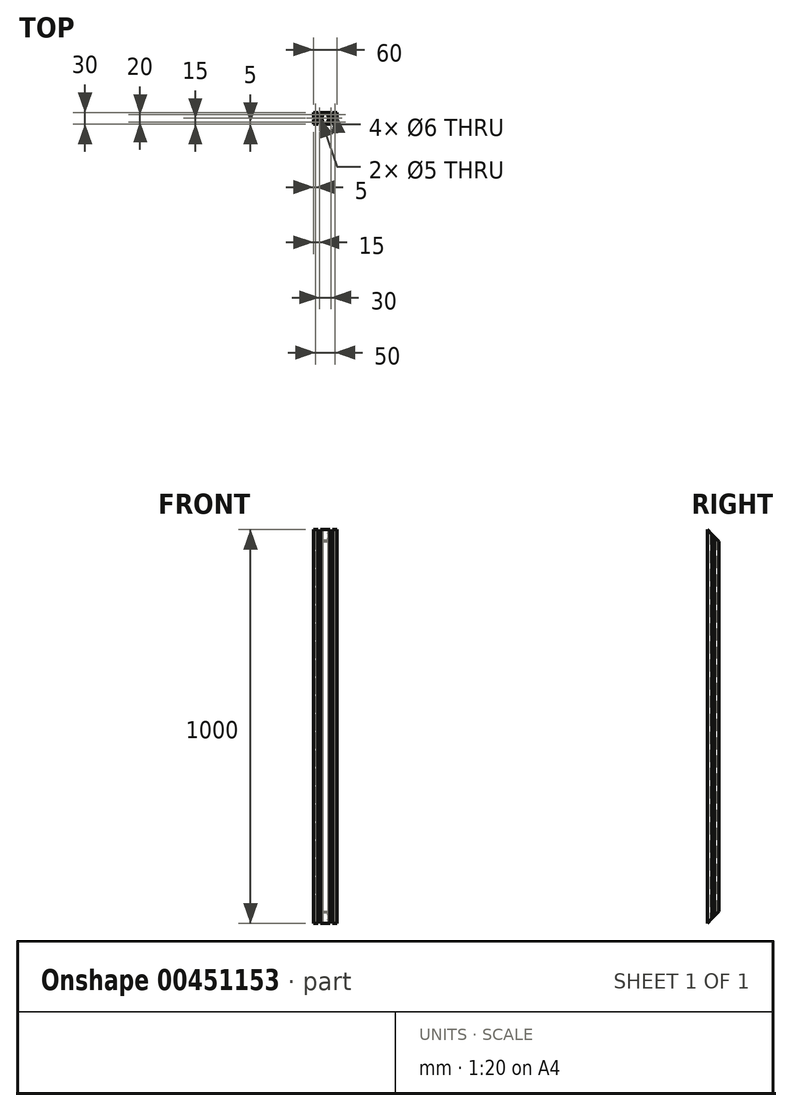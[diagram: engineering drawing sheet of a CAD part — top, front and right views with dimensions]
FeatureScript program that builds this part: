
annotation { "Feature Type Name" : "Feature", "Feature Type Description" : "" }
export const myFeature = defineFeature(function(context is Context, id is Id, definition is map)
    precondition{}
    {
        {
            var Q0;
            Q0=qCreatedBy(makeId("Top.planeOp"),FACE);
            var sketch = newSketch(context, id + "F0", { "sketchPlane" : qUnion([Q0])});
            skLineSegment(sketch, "E0.bottom", {"start": v(30, -15) * mm, "end": v(-30, -15) * mm});
            skLineSegment(sketch, "E0.top", {"start": v(30, 15) * mm, "end": v(-30, 15) * mm});
            skLineSegment(sketch, "E0.left", {"start": v(30, -15) * mm, "end": v(30, 15) * mm});
            skLineSegment(sketch, "E0.right", {"start": v(-30, -15) * mm, "end": v(-30, 15) * mm});
            skPoint(sketch, "E0.middle", {"position": v(0, 0) * mm});
            skLineSegment(sketch, "E1.top", {"start": v(-11.85, 15) * mm, "end": v(-18.15, 15) * mm});
            skLineSegment(sketch, "E1.left", {"start": v(-11.85, 12.5) * mm, "end": v(-11.85, 15) * mm});
            skLineSegment(sketch, "E1.right", {"start": v(-18.15, 12.5) * mm, "end": v(-18.15, 15) * mm});
            skPoint(sketch, "E1.middle", {"position": v(-15, 13.75) * mm});
            skLineSegment(sketch, "E2.bottom", {"start": v(-9.85, 12.5) * mm, "end": v(-11.85, 12.5) * mm});
            skLineSegment(sketch, "E2.left", {"start": v(-9.85, 12.5) * mm, "end": v(-9.85, 6.55) * mm});
            skLineSegment(sketch, "E2.right", {"start": v(-20.15, 12.5) * mm, "end": v(-20.15, 6.55) * mm});
            skPoint(sketch, "E2.middle", {"position": v(-15, 9.52) * mm});
            skArc(sketch, "E3", {"start": v(-20.15, 6.55) * mm, "mid": v(-15, 4.5) * mm, "end": v(-9.85, 6.55) * mm});
            skPoint(sketch, "E4.MirrorP", {"position": v(15, 9.52) * mm});
            skPoint(sketch, "E5.MirrorP", {"position": v(15, 13.75) * mm});
            skLineSegment(sketch, "E6.MirrorCS", {"start": v(11.85, 12.5) * mm, "end": v(11.85, 15) * mm});
            skLineSegment(sketch, "E7.MirrorCS", {"start": v(18.15, 12.5) * mm, "end": v(18.15, 15) * mm});
            skLineSegment(sketch, "E8.MirrorCS", {"start": v(9.85, 12.5) * mm, "end": v(11.85, 12.5) * mm});
            skLineSegment(sketch, "E9.MirrorCS", {"start": v(9.85, 12.5) * mm, "end": v(9.85, 6.55) * mm});
            skArc(sketch, "E10.MirrorCS", {"start": v(20.15, 6.55) * mm, "mid": v(15, 4.5) * mm, "end": v(9.85, 6.55) * mm});
            skLineSegment(sketch, "E11.MirrorCS", {"start": v(20.15, 12.5) * mm, "end": v(20.15, 6.55) * mm});
            skLineSegment(sketch, "E12.MirrorCS", {"start": v(11.85, 15) * mm, "end": v(18.15, 15) * mm});
            skLineSegment(sketch, "E13.trimOffspring", {"start": v(-18.15, 12.5) * mm, "end": v(-20.15, 12.5) * mm});
            skLineSegment(sketch, "E14.trimOffspring", {"start": v(18.15, 12.5) * mm, "end": v(20.15, 12.5) * mm});
            skCircle(sketch, "E15", {"center": v(-15, 0) * mm, "radius": 2.5 * mm});
            skCircle(sketch, "E16", {"center": v(-25, 10) * mm, "radius": 3 * mm});
            skCircle(sketch, "E17.MirrorC", {"center": v(25, 10) * mm, "radius": 3 * mm});
            skCircle(sketch, "E18.MirrorC", {"center": v(25, -10) * mm, "radius": 3 * mm});
            skCircle(sketch, "E19.MirrorC", {"center": v(-25, -10) * mm, "radius": 3 * mm});
            skCircle(sketch, "E20.MirrorC", {"center": v(15, 0) * mm, "radius": 2.5 * mm});
            skLineSegment(sketch, "E21", {"start": v(-7, 12.5) * mm, "end": v(0, 12.5) * mm});
            skLineSegment(sketch, "E22", {"start": v(-7, 12.5) * mm, "end": v(-7, 7) * mm});
            skLineSegment(sketch, "E23", {"start": v(-10, 0) * mm, "end": v(-7, 7) * mm});
            skLineSegment(sketch, "E24.MirrorCS", {"start": v(10, 0) * mm, "end": v(7, 7) * mm});
            skLineSegment(sketch, "E25.MirrorCS", {"start": v(7, 12.5) * mm, "end": v(0, 12.5) * mm});
            skLineSegment(sketch, "E26.MirrorCS", {"start": v(7, 12.5) * mm, "end": v(7, 7) * mm});
            skLineSegment(sketch, "E27.MirrorCS", {"start": v(-18.15, -12.5) * mm, "end": v(-20.15, -12.5) * mm});
            skLineSegment(sketch, "E28.MirrorCS", {"start": v(-9.85, -12.5) * mm, "end": v(-11.85, -12.5) * mm});
            skLineSegment(sketch, "E29.MirrorCS", {"start": v(-9.85, -12.5) * mm, "end": v(-9.85, -6.55) * mm});
            skPoint(sketch, "E30.MirrorP", {"position": v(-15, -13.75) * mm});
            skPoint(sketch, "E31.MirrorP", {"position": v(-15, -9.52) * mm});
            skLineSegment(sketch, "E32.MirrorCS", {"start": v(-18.15, -12.5) * mm, "end": v(-18.15, -15) * mm});
            skLineSegment(sketch, "E33.MirrorCS", {"start": v(-11.85, -15) * mm, "end": v(-18.15, -15) * mm});
            skLineSegment(sketch, "E34.MirrorCS", {"start": v(-20.15, -12.5) * mm, "end": v(-20.15, -6.55) * mm});
            skLineSegment(sketch, "E35.MirrorCS", {"start": v(-11.85, -12.5) * mm, "end": v(-11.85, -15) * mm});
            skArc(sketch, "E36.MirrorCS", {"start": v(-20.15, -6.55) * mm, "mid": v(-15, -4.5) * mm, "end": v(-9.85, -6.55) * mm});
            skLineSegment(sketch, "E37.MirrorCS", {"start": v(18.15, -12.5) * mm, "end": v(20.15, -12.5) * mm});
            skLineSegment(sketch, "E38.MirrorCS", {"start": v(9.85, -12.5) * mm, "end": v(11.85, -12.5) * mm});
            skPoint(sketch, "E39.MirrorP", {"position": v(15, -13.75) * mm});
            skPoint(sketch, "E40.MirrorP", {"position": v(15, -9.52) * mm});
            skLineSegment(sketch, "E41.MirrorCS", {"start": v(18.15, -12.5) * mm, "end": v(18.15, -15) * mm});
            skArc(sketch, "E42.MirrorCS", {"start": v(20.15, -6.55) * mm, "mid": v(15, -4.5) * mm, "end": v(9.85, -6.55) * mm});
            skLineSegment(sketch, "E43.MirrorCS", {"start": v(9.85, -12.5) * mm, "end": v(9.85, -6.55) * mm});
            skLineSegment(sketch, "E44.MirrorCS", {"start": v(11.85, -12.5) * mm, "end": v(11.85, -15) * mm});
            skLineSegment(sketch, "E45.MirrorCS", {"start": v(11.85, -15) * mm, "end": v(18.15, -15) * mm});
            skLineSegment(sketch, "E46.MirrorCS", {"start": v(20.15, -12.5) * mm, "end": v(20.15, -6.55) * mm});
            skLineSegment(sketch, "E47.MirrorCS", {"start": v(10, 0) * mm, "end": v(7, -7) * mm});
            skLineSegment(sketch, "E48.MirrorCS", {"start": v(7, -12.5) * mm, "end": v(7, -7) * mm});
            skLineSegment(sketch, "E49.MirrorCS", {"start": v(7, -12.5) * mm, "end": v(0, -12.5) * mm});
            skLineSegment(sketch, "E50.MirrorCS", {"start": v(-7, -12.5) * mm, "end": v(0, -12.5) * mm});
            skLineSegment(sketch, "E51.MirrorCS", {"start": v(-10, 0) * mm, "end": v(-7, -7) * mm});
            skLineSegment(sketch, "E52.MirrorCS", {"start": v(-7, -12.5) * mm, "end": v(-7, -7) * mm});
            skLineSegment(sketch, "E53.top", {"start": v(-30, 3.15) * mm, "end": v(-30, -3.15) * mm});
            skLineSegment(sketch, "E53.left", {"start": v(-27.5, 3.15) * mm, "end": v(-30, 3.15) * mm});
            skLineSegment(sketch, "E53.right", {"start": v(-27.5, -3.15) * mm, "end": v(-30, -3.15) * mm});
            skLineSegment(sketch, "E54.bottom", {"start": v(-27.5, 5.15) * mm, "end": v(-27.5, 3.15) * mm});
            skLineSegment(sketch, "E54.left", {"start": v(-27.5, 5.15) * mm, "end": v(-21.55, 5.15) * mm});
            skLineSegment(sketch, "E54.right", {"start": v(-27.5, -5.15) * mm, "end": v(-21.55, -5.15) * mm});
            skArc(sketch, "E55", {"start": v(-21.55, -5.15) * mm, "mid": v(-19.5, 0) * mm, "end": v(-21.55, 5.15) * mm});
            skLineSegment(sketch, "E56.trimOffspring", {"start": v(-27.5, -3.15) * mm, "end": v(-27.5, -5.15) * mm});
            skArc(sketch, "E57.MirrorCS", {"start": v(21.55, -5.15) * mm, "mid": v(19.5, 0) * mm, "end": v(21.55, 5.15) * mm});
            skLineSegment(sketch, "E58.MirrorCS", {"start": v(27.5, -5.15) * mm, "end": v(21.55, -5.15) * mm});
            skLineSegment(sketch, "E59.MirrorCS", {"start": v(30, 3.15) * mm, "end": v(30, -3.15) * mm});
            skLineSegment(sketch, "E60.MirrorCS", {"start": v(27.5, -3.15) * mm, "end": v(30, -3.15) * mm});
            skLineSegment(sketch, "E61.MirrorCS", {"start": v(27.5, 5.15) * mm, "end": v(27.5, 3.15) * mm});
            skLineSegment(sketch, "E62.MirrorCS", {"start": v(27.5, 3.15) * mm, "end": v(30, 3.15) * mm});
            skLineSegment(sketch, "E63.MirrorCS", {"start": v(27.5, 5.15) * mm, "end": v(21.55, 5.15) * mm});
            skLineSegment(sketch, "E64.MirrorCS", {"start": v(27.5, -3.15) * mm, "end": v(27.5, -5.15) * mm});
            skSolve(sketch);
        }
        {
            var Q0;
            {var subQ30=sQuery(id+"F0.wireOp",EDGE,"E1.left");Q0=makeQuery(id+"F0.imprint","IMPRINT",FACE,{"disambiguationData":[TD([[makeQuery(id+"F0.imprint","IMPRINT",EDGE,{"derivedFrom":subQ30}),-1.0]])]});}
            extrude(context, id + "F1", {"entities" : qUnion([Q0]), "offsetDistance" : 25 * mm, "depth" : 1000 * mm});
        }
        {
            var Q0;
            Q0=makeQuery(id+"F1.opExtrude","SWEPT_EDGE",EDGE,{"disambiguationData":[OSD([sQuery(id+"F0.wireOp",EDGE,"E21"),sQuery(id+"F0.wireOp",EDGE,"E22")])]});
            var Q1;
            Q1=makeQuery(id+"F1.opExtrude","SWEPT_EDGE",EDGE,{"disambiguationData":[OSD([sQuery(id+"F0.wireOp",EDGE,"E25.MirrorCS"),sQuery(id+"F0.wireOp",EDGE,"E26.MirrorCS")])]});
            var Q2;
            Q2=makeQuery(id+"F1.opExtrude","SWEPT_EDGE",EDGE,{"disambiguationData":[OSD([sQuery(id+"F0.wireOp",EDGE,"840db5bc-c403-45cd-90c7-254e62d9e8c5.3.2"),sQuery(id+"F0.wireOp",EDGE,"840db5bc-c403-45cd-90c7-254e62d9e8c5.3.3")])]});
            var Q3;
            Q3=makeQuery(id+"F1.opExtrude","SWEPT_EDGE",EDGE,{"disambiguationData":[OSD([sQuery(id+"F0.wireOp",EDGE,"840db5bc-c403-45cd-90c7-254e62d9e8c5.3.4"),sQuery(id+"F0.wireOp",EDGE,"840db5bc-c403-45cd-90c7-254e62d9e8c5.3.5")])]});
            var Q4;
            Q4=makeQuery(id+"F1.opExtrude","SWEPT_EDGE",EDGE,{"disambiguationData":[OSD([sQuery(id+"F0.wireOp",EDGE,"840db5bc-c403-45cd-90c7-254e62d9e8c5.1.4"),sQuery(id+"F0.wireOp",EDGE,"840db5bc-c403-45cd-90c7-254e62d9e8c5.1.5")])]});
            var Q5;
            Q5=makeQuery(id+"F1.opExtrude","SWEPT_EDGE",EDGE,{"disambiguationData":[OSD([sQuery(id+"F0.wireOp",EDGE,"840db5bc-c403-45cd-90c7-254e62d9e8c5.1.2"),sQuery(id+"F0.wireOp",EDGE,"840db5bc-c403-45cd-90c7-254e62d9e8c5.1.3")])]});
            var Q6;
            Q6=makeQuery(id+"F1.opExtrude","SWEPT_EDGE",EDGE,{"disambiguationData":[OSD([sQuery(id+"F0.wireOp",EDGE,"840db5bc-c403-45cd-90c7-254e62d9e8c5.2.2"),sQuery(id+"F0.wireOp",EDGE,"840db5bc-c403-45cd-90c7-254e62d9e8c5.2.3")])]});
            var Q7;
            Q7=makeQuery(id+"F1.opExtrude","SWEPT_EDGE",EDGE,{"disambiguationData":[OSD([sQuery(id+"F0.wireOp",EDGE,"840db5bc-c403-45cd-90c7-254e62d9e8c5.2.4"),sQuery(id+"F0.wireOp",EDGE,"840db5bc-c403-45cd-90c7-254e62d9e8c5.2.5")])]});
            fillet(context, id + "F2", {"entities" : qUnion([Q0, Q1, Q2, Q3, Q4, Q5, Q6, Q7]), "radius" : 2 * mm, "tangentPropagation" : true, "allowEdgeOverflow" : false});
        }
        {
            var Q0;
            Q0=makeQuery(id+"F1.opExtrude","SWEPT_EDGE",EDGE,{"disambiguationData":[OSD([sQuery(id+"F0.wireOp",EDGE,"DFmKlNwq-wdCH-8nxe-YtyU-4GV9lN6q6mBF"),sQuery(id+"F0.wireOp",EDGE,"E23")])]});
            var Q1;
            Q1=makeQuery(id+"F1.opExtrude","SWEPT_EDGE",EDGE,{"disambiguationData":[OSD([sQuery(id+"F0.wireOp",EDGE,"666cdc41-9f22-4022-b962-67eb0134baf70.MirrorCS"),sQuery(id+"F0.wireOp",EDGE,"E24.MirrorCS")])]});
            var Q2;
            Q2=makeQuery(id+"F1.opExtrude","SWEPT_EDGE",EDGE,{"disambiguationData":[OSD([sQuery(id+"F0.wireOp",EDGE,"840db5bc-c403-45cd-90c7-254e62d9e8c5.3.0"),sQuery(id+"F0.wireOp",EDGE,"840db5bc-c403-45cd-90c7-254e62d9e8c5.3.1")])]});
            var Q3;
            Q3=makeQuery(id+"F1.opExtrude","SWEPT_EDGE",EDGE,{"disambiguationData":[OSD([sQuery(id+"F0.wireOp",EDGE,"840db5bc-c403-45cd-90c7-254e62d9e8c5.1.6"),sQuery(id+"F0.wireOp",EDGE,"840db5bc-c403-45cd-90c7-254e62d9e8c5.1.7")])]});
            var Q4;
            Q4=makeQuery(id+"F1.opExtrude","SWEPT_EDGE",EDGE,{"disambiguationData":[OSD([sQuery(id+"F0.wireOp",EDGE,"840db5bc-c403-45cd-90c7-254e62d9e8c5.1.0"),sQuery(id+"F0.wireOp",EDGE,"840db5bc-c403-45cd-90c7-254e62d9e8c5.1.1")])]});
            var Q5;
            Q5=makeQuery(id+"F1.opExtrude","SWEPT_EDGE",EDGE,{"disambiguationData":[OSD([sQuery(id+"F0.wireOp",EDGE,"840db5bc-c403-45cd-90c7-254e62d9e8c5.3.6"),sQuery(id+"F0.wireOp",EDGE,"840db5bc-c403-45cd-90c7-254e62d9e8c5.3.7")])]});
            var Q6;
            Q6=makeQuery(id+"F1.opExtrude","SWEPT_EDGE",EDGE,{"disambiguationData":[OSD([sQuery(id+"F0.wireOp",EDGE,"840db5bc-c403-45cd-90c7-254e62d9e8c5.2.0"),sQuery(id+"F0.wireOp",EDGE,"840db5bc-c403-45cd-90c7-254e62d9e8c5.2.1")])]});
            var Q7;
            Q7=makeQuery(id+"F1.opExtrude","SWEPT_EDGE",EDGE,{"disambiguationData":[OSD([sQuery(id+"F0.wireOp",EDGE,"840db5bc-c403-45cd-90c7-254e62d9e8c5.2.6"),sQuery(id+"F0.wireOp",EDGE,"840db5bc-c403-45cd-90c7-254e62d9e8c5.2.7")])]});
            fillet(context, id + "F3", {"entities" : qUnion([Q0, Q1, Q2, Q3, Q4, Q5, Q6, Q7]), "radius" : 7 * mm, "tangentPropagation" : true, "allowEdgeOverflow" : false});
        }
        {
            var Q0;
            Q0=qCreatedBy(makeId("Right.planeOp"),FACE);
            var sketch = newSketch(context, id + "F4", { "sketchPlane" : qUnion([Q0])});
            skLineSegment(sketch, "E65", {"start": v(-15, 0) * mm, "end": v(15, 30) * mm});
            skLineSegment(sketch, "E66", {"start": v(15, 30) * mm, "end": v(15, 0) * mm});
            skLineSegment(sketch, "E67", {"start": v(15, 0) * mm, "end": v(-15, 0) * mm});
            skLineSegment(sketch, "E68", {"start": v(-15, 1000) * mm, "end": v(15, 1000) * mm});
            skLineSegment(sketch, "E69", {"start": v(15, 1000) * mm, "end": v(15, 970) * mm});
            skLineSegment(sketch, "E70", {"start": v(15, 970) * mm, "end": v(-15, 1000) * mm});
            skSolve(sketch);
        }
        {
            var Q0;
            Q0=qSketchRegion(id+"F4",true);
            extrude(context, id + "F5", {"entities" : qUnion([Q0]), "operationType" : NewBodyOperationType.REMOVE, "oppositeDirection" : true, "depth" : 60 * mm, "offsetDistance" : 25 * mm, "symmetric" : true});
        }
    });
